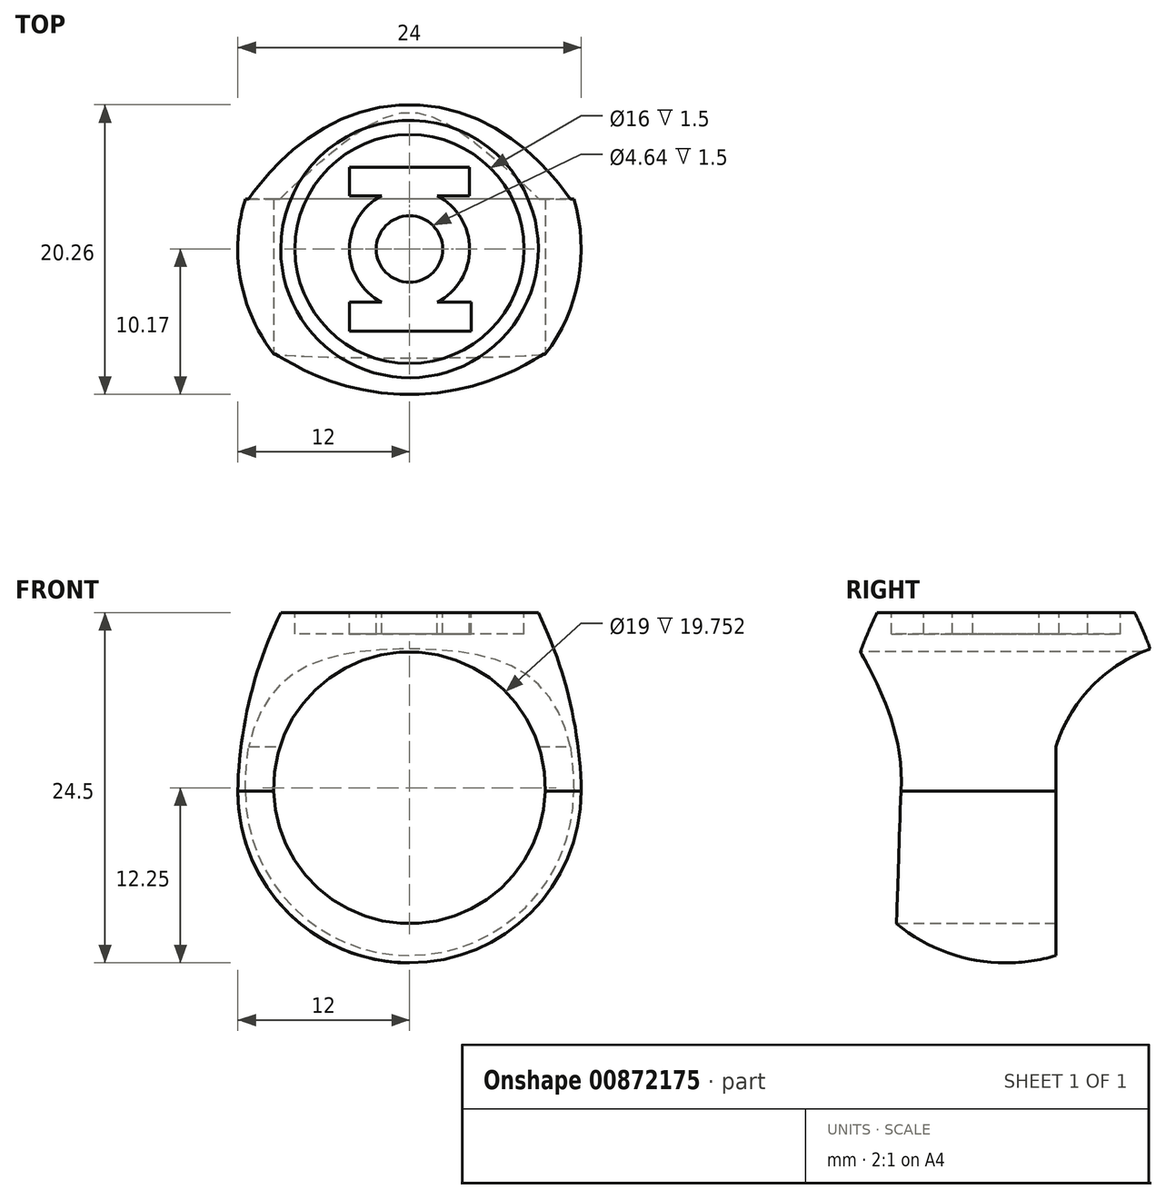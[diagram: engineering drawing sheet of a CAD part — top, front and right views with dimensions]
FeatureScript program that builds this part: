
annotation { "Feature Type Name" : "Feature", "Feature Type Description" : "" }
export const myFeature = defineFeature(function(context is Context, id is Id, definition is map)
    precondition{}
    {
        {
            var Q0;
            Q0=qCreatedBy(makeId("Front.planeOp"),FACE);
            var sketch = newSketch(context, id + "F0", { "sketchPlane" : qUnion([Q0])});
            skLineSegment(sketch, "E0", {"start": v(0, -24.5) * mm, "end": v(0, 0) * mm});
            skPoint(sketch, "E1.0", {"position": v(0, 0) * mm});
            skLineSegment(sketch, "E2", {"start": v(0, 0) * mm, "end": v(-9, 0) * mm});
            skPoint(sketch, "E3", {"position": v(0, -12.5) * mm});
            skLineSegment(sketch, "E4", {"start": v(0, -12.5) * mm, "end": v(-12, -12.5) * mm});
            skArc(sketch, "E5", {"start": v(-12, -12.5) * mm, "mid": v(-8.49, -20.99) * mm, "end": v(0, -24.5) * mm});
            skArc(sketch, "E6", {"start": v(-9, 0) * mm, "mid": v(-11.18, -6.09) * mm, "end": v(-12, -12.5) * mm});
            skSolve(sketch);
        }
        {
            var Q0;
            Q0=qSketchRegion(id+"F0",true);
            var Q1;
            Q1=sQuery(id+"F0.wireOp",EDGE,"E0");
            revolve(context, id + "F1", {"surfaceOperationType" : NewSurfaceOperationType.NEW, "entities" : qUnion([Q0]), "axis" : qUnion([Q1]), "revolveType" : RevolveType.FULL});
        }
        {
            var Q0;
            Q0=qCreatedBy(makeId("Front.planeOp"),FACE);
            var sketch = newSketch(context, id + "F2", { "sketchPlane" : qUnion([Q0])});
            skPoint(sketch, "E7", {"position": v(0, -12.25) * mm});
            skCircle(sketch, "E8", {"center": v(0, -12.25) * mm, "radius": 9.5 * mm});
            skSolve(sketch);
        }
        {
            var Q0;
            Q0=qSketchRegion(id+"F2",true);
            extrude(context, id + "F3", {"entities" : qUnion([Q0]), "operationType" : NewBodyOperationType.REMOVE, "endBound" : BoundingType.SYMMETRIC, "oppositeDirection" : true, "depth" : 25.4 * mm, "offsetDistance" : 25.4 * mm});
        }
        {
            var Q0;
            Q0=qCreatedBy(makeId("Top.planeOp"),FACE);
            var sketch = newSketch(context, id + "F4", { "sketchPlane" : qUnion([Q0])});
            skCircle(sketch, "E9", {"center": v(0, 0) * mm, "radius": 8 * mm});
            skCircle(sketch, "E10", {"center": v(0, 0) * mm, "radius": 2.32 * mm});
            skLineSegment(sketch, "E11", {"start": v(0, 5.73) * mm, "end": v(4.2, 5.73) * mm});
            skLineSegment(sketch, "E12", {"start": v(0, 0) * mm, "end": v(-4.2, 0) * mm});
            skCircle(sketch, "E13", {"center": v(0, 0) * mm, "radius": 4.2 * mm});
            skPoint(sketch, "E14", {"position": v(1.93, 3.73) * mm});
            skLineSegment(sketch, "E15", {"start": v(0, 5.73) * mm, "end": v(-4.2, 5.73) * mm});
            skLineSegment(sketch, "E16", {"start": v(-4.2, 5.73) * mm, "end": v(-4.2, 3.73) * mm});
            skPoint(sketch, "E17", {"position": v(-1.94, 3.73) * mm});
            skLineSegment(sketch, "E18", {"start": v(-1.94, 3.73) * mm, "end": v(-4.2, 3.73) * mm});
            skLineSegment(sketch, "E19", {"start": v(0, -5.73) * mm, "end": v(-4.2, -5.73) * mm});
            skLineSegment(sketch, "E20", {"start": v(-4.2, -5.73) * mm, "end": v(-4.2, -3.73) * mm});
            skLineSegment(sketch, "E21", {"start": v(0, -5.73) * mm, "end": v(4.33, -5.73) * mm});
            skLineSegment(sketch, "E22", {"start": v(-4.2, -3.73) * mm, "end": v(-1.94, -3.73) * mm});
            skLineSegment(sketch, "E23", {"start": v(4.33, -5.73) * mm, "end": v(4.33, -3.73) * mm});
            skLineSegment(sketch, "E24", {"start": v(4.33, -3.73) * mm, "end": v(1.94, -3.73) * mm});
            skLineSegment(sketch, "E25", {"start": v(4.2, 5.73) * mm, "end": v(4.2, 3.73) * mm});
            skLineSegment(sketch, "E26", {"start": v(4.2, 3.73) * mm, "end": v(1.93, 3.73) * mm});
            skSolve(sketch);
        }
        {
            var Q0;
            Q0=makeQuery(id+"F4.imprint","IMPRINT",FACE,{"disambiguationData":[TD([[makeQuery(id+"F4.imprint","IMPRINT",EDGE,{"derivedFrom":sQuery(id+"F4.wireOp",EDGE,"E9")}),1.0]])]});
            var Q1;
            Q1=makeQuery(id+"F4.imprint","IMPRINT",FACE,{"disambiguationData":[TD([[makeQuery(id+"F4.imprint","IMPRINT",EDGE,{"derivedFrom":sQuery(id+"F4.wireOp",EDGE,"E10")}),1.0]])]});
            extrude(context, id + "F5", {"entities" : qUnion([Q0, Q1]), "operationType" : NewBodyOperationType.REMOVE, "oppositeDirection" : true, "depth" : 1.5 * mm, "offsetDistance" : 25.4 * mm});
        }
        {
            var Q0;
            Q0=qCreatedBy(makeId("Right.planeOp"),FACE);
            var sketch = newSketch(context, id + "F6", { "sketchPlane" : qUnion([Q0])});
            skLineSegment(sketch, "E27", {"start": v(0, 0) * mm, "end": v(9, 0) * mm});
            skLineSegment(sketch, "E28", {"start": v(3.5, -26.5) * mm, "end": v(11.74, -26.5) * mm});
            skLineSegment(sketch, "E29", {"start": v(11.74, -2.5) * mm, "end": v(11.74, -26.5) * mm});
            skLineSegment(sketch, "E30", {"start": v(11.74, -2.5) * mm, "end": v(11.74, -12.5) * mm});
            skArc(sketch, "E31", {"start": v(10.25, -2.5) * mm, "mid": v(6.04, -5.13) * mm, "end": v(3.5, -9.39) * mm});
            skLineSegment(sketch, "E32", {"start": v(3.5, -26.5) * mm, "end": v(3.5, -9.39) * mm});
            skLineSegment(sketch, "E33", {"start": v(0, 0) * mm, "end": v(-9, 0) * mm});
            skPoint(sketch, "E34.endSnap0", {"position": v(-4.5, 0) * mm});
            skLineSegment(sketch, "E35", {"start": v(10.25, -2.5) * mm, "end": v(11.74, -2.5) * mm});
            skSolve(sketch);
        }
        {
            var Q0;
            Q0=makeQuery(id+"F6.imprint","IMPRINT",FACE,{"disambiguationData":[TD([[makeQuery(id+"F6.imprint","IMPRINT",EDGE,{"derivedFrom":sQuery(id+"F6.wireOp",EDGE,"oE8o5vbM-vYRr-qUDM-GR20-g5ichJYpVI2U")}),-1.0]])]});
            var Q1;
            Q1=makeQuery(id+"F6.imprint","IMPRINT",FACE,{"disambiguationData":[TD([[makeQuery(id+"F6.imprint","IMPRINT",EDGE,{"derivedFrom":sQuery(id+"F6.wireOp",EDGE,"E28")}),1.0]])]});
            extrude(context, id + "F7", {"entities" : qUnion([Q0, Q1]), "operationType" : NewBodyOperationType.REMOVE, "endBound" : BoundingType.SYMMETRIC, "oppositeDirection" : true, "depth" : 25.4 * mm, "offsetDistance" : 25.4 * mm});
        }
    });
